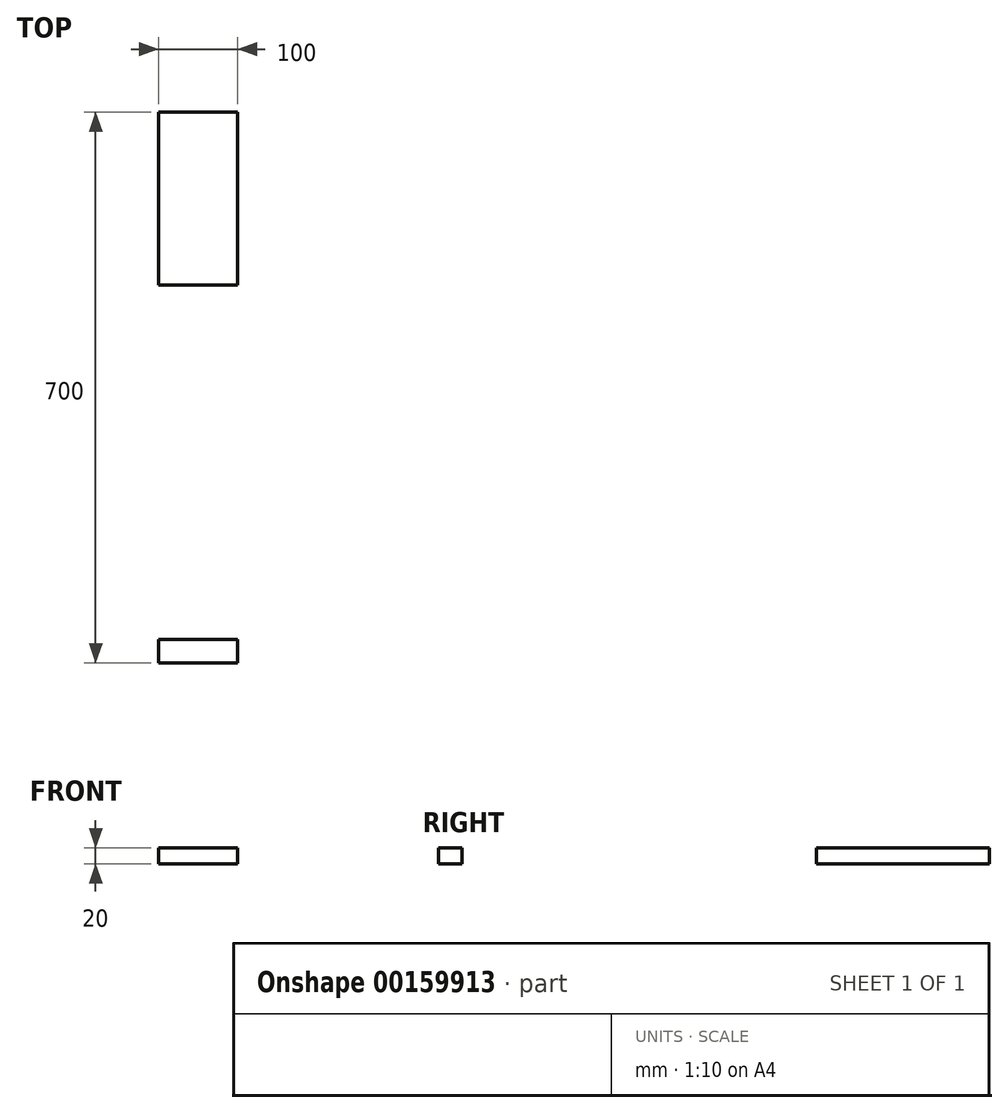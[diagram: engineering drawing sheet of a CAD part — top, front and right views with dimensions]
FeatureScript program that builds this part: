
annotation { "Feature Type Name" : "Feature", "Feature Type Description" : "" }
export const myFeature = defineFeature(function(context is Context, id is Id, definition is map)
    precondition{}
    {
        {
            assignVariable(context, id + "F0", {"name" : "t", "anyValue" : 20 * mm});
        }
        {
            var Q0;
            Q0=qCreatedBy(makeId("Top.planeOp"),FACE);
            var sketch = newSketch(context, id + "F1", { "sketchPlane" : qUnion([Q0])});
            skLineSegment(sketch, "E0.bottom", {"start": v(935, -350) * mm, "end": v(-935, -350) * mm});
            skLineSegment(sketch, "E0.top", {"start": v(935, 350) * mm, "end": v(-935, 350) * mm});
            skLineSegment(sketch, "E0.left", {"start": v(935, -350) * mm, "end": v(935, 350) * mm});
            skLineSegment(sketch, "E0.right", {"start": v(-935, -350) * mm, "end": v(-935, 350) * mm});
            skPoint(sketch, "E0.middle", {"position": v(0, 0) * mm});
            skLineSegment(sketch, "E1.bottom", {"start": v(-935, -350) * mm, "end": v(-835, -350) * mm});
            skLineSegment(sketch, "E1.top", {"start": v(-935, -320) * mm, "end": v(-835, -320) * mm});
            skLineSegment(sketch, "E1.left", {"start": v(-935, -350) * mm, "end": v(-935, -320) * mm});
            skLineSegment(sketch, "E1.right", {"start": v(-835, -350) * mm, "end": v(-835, -320) * mm});
            skLineSegment(sketch, "E2.bottom", {"start": v(-935, 350) * mm, "end": v(-835, 350) * mm});
            skLineSegment(sketch, "E2.top", {"start": v(-935, 130) * mm, "end": v(-835, 130) * mm});
            skLineSegment(sketch, "E2.left", {"start": v(-935, 350) * mm, "end": v(-935, 130) * mm});
            skLineSegment(sketch, "E2.right", {"start": v(-835, 350) * mm, "end": v(-835, 130) * mm});
            skLineSegment(sketch, "E3.MirrorCS", {"start": v(835, 350) * mm, "end": v(835, 130) * mm});
            skLineSegment(sketch, "E4.MirrorCS", {"start": v(935, 130) * mm, "end": v(835, 130) * mm});
            skLineSegment(sketch, "E5.MirrorCS", {"start": v(935, -320) * mm, "end": v(835, -320) * mm});
            skLineSegment(sketch, "E6.MirrorCS", {"start": v(835, -350) * mm, "end": v(835, -320) * mm});
            skSolve(sketch);
        }
        {
            var Q0;
            Q0=makeQuery(id+"F1.imprint","IMPRINT",FACE,{"disambiguationData":[TD([[makeQuery(id+"F1.imprint","IMPRINT",EDGE,{"derivedFrom":sQuery(id+"F1.wireOp",EDGE,"E0.right")}),-1.0]])]});
            extrude(context, id + "F2", {"entities" : qUnion([Q0]), "depth" : getVariable(context, 't')});
        }
    });
